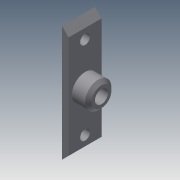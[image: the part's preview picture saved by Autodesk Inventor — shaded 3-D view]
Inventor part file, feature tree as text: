
AUTODESK INVENTOR PART (.ipt)
format: ipt  version: 2015 (Build 190159000, 159)  size: 109,568 bytes
history: native  units: mm
features: extrude x4, sketch x4, chamfer x2
ambient origin geometry x8: Origin, YZ Plane, XZ Plane, XY Plane, X Axis, Y Axis, Z Axis, Center Point
bodies: Solid1 (feature_tree)
feature tree (10):
  extrude  "Extrusion1"  Depth=10.0mm
  extrude  "Extrusion2"  Depth=2.0mm
  extrude  "Extrusion3"  Depth=4.0mm
  extrude  "Extrusion4"  Depth=5.0mm
  chamfer  "Chamfer1"  Distance=5.0mm
  chamfer  "Chamfer2"  Distance=3.0mm
  sketch  "Sketch1"  dims[d0=35.186mm d2=10.0mm]
  sketch  "Sketch2"  dims[d3=2.0mm d4=0.0mm d5=8.0mm]
  sketch  "Sketch3"  dims[d6=5.0mm d7=0.0mm d8=4.0mm]
  sketch  "Sketch4"  dims[d9=7.0mm d10=0.0mm d11=5.0mm d12=5.0mm d13=3.0mm d14=3.0mm d15=2.0mm d16=0.0mm d17=1.0mm d18=2.0mm d19=45.0deg d20=2.0mm d21=2.0mm d22=45.0deg]
